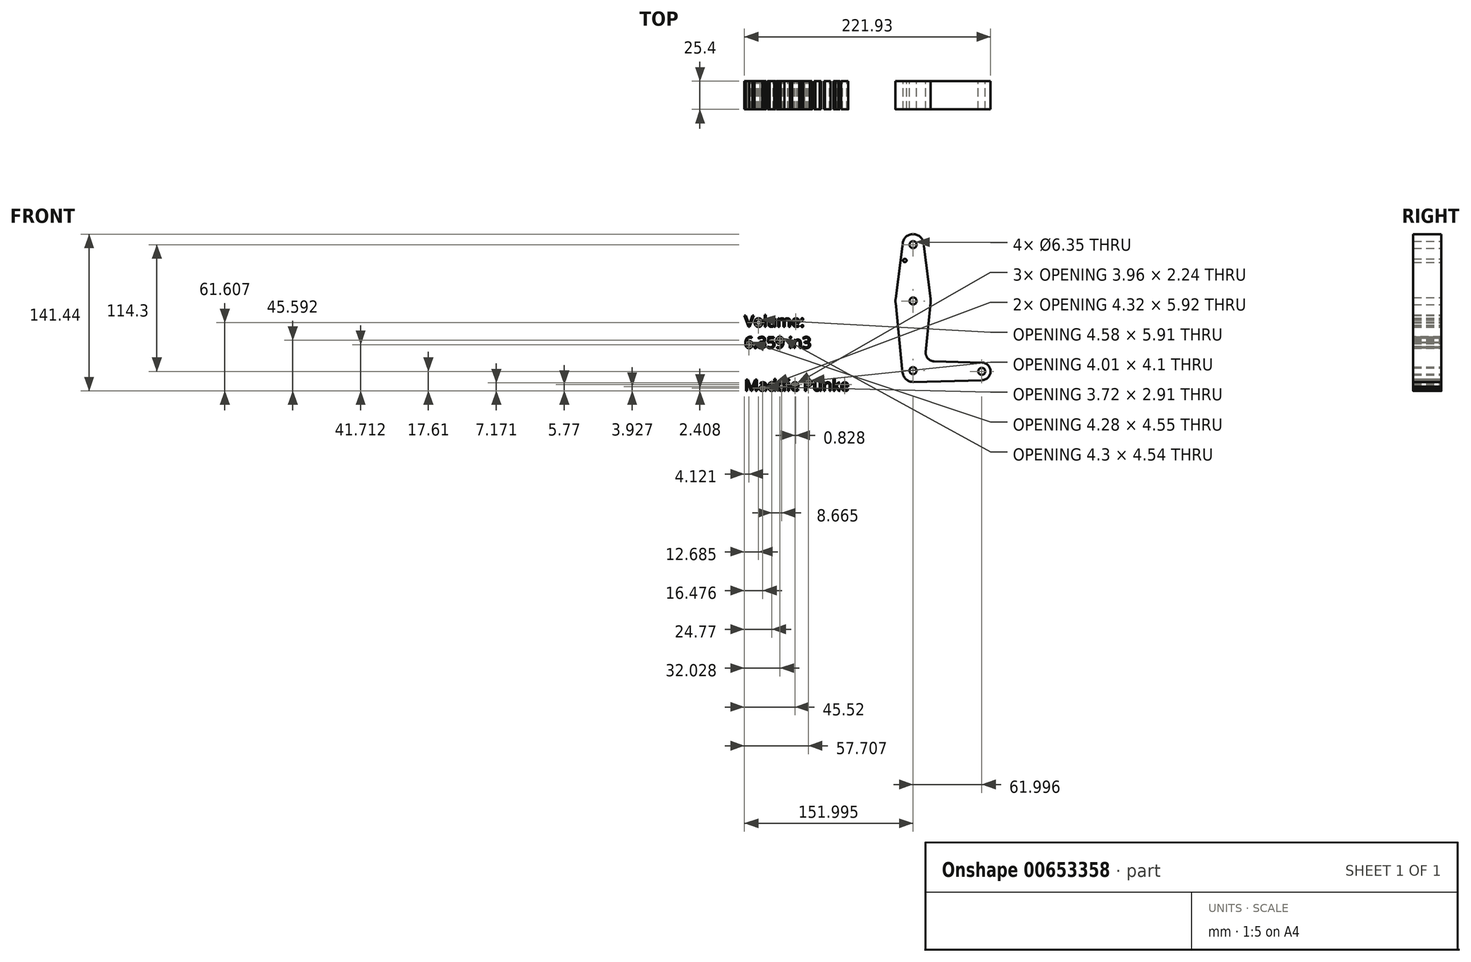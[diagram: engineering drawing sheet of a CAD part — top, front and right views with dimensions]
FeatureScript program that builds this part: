
annotation { "Feature Type Name" : "Feature", "Feature Type Description" : "" }
export const myFeature = defineFeature(function(context is Context, id is Id, definition is map)
    precondition{}
    {
        {
            var Q0;
            Q0=qCreatedBy(makeId("Front.planeOp"),FACE);
            var sketch = newSketch(context, id + "F0", { "sketchPlane" : qUnion([Q0])});
            skLineSegment(sketch, "E0", {"start": v(-2.44, 74.08) * mm, "end": v(-2.44, -40.22) * mm});
            skLineSegment(sketch, "E1", {"start": v(-2.44, -40.22) * mm, "end": v(59.47, -40.22) * mm});
            skCircle(sketch, "E2", {"center": v(-2.44, 74.08) * mm, "radius": 9.53 * mm});
            skCircle(sketch, "E3", {"center": v(-2.44, 23.28) * mm, "radius": 15.88 * mm});
            skCircle(sketch, "E4", {"center": v(-2.44, -40.22) * mm, "radius": 9.53 * mm});
            skCircle(sketch, "E5", {"center": v(59.47, -40.22) * mm, "radius": 7.94 * mm});
            skLineSegment(sketch, "E6", {"start": v(-11.9, 75.27) * mm, "end": v(-18.2, 25.26) * mm});
            skLineSegment(sketch, "E7", {"start": v(-18.24, 21.7) * mm, "end": v(-11.92, -41.17) * mm});
            skLineSegment(sketch, "E8", {"start": v(-2.2, -49.74) * mm, "end": v(59.67, -48.15) * mm});
            skCircle(sketch, "E9", {"center": v(-2.44, 74.08) * mm, "radius": 3.18 * mm});
            skCircle(sketch, "E10", {"center": v(-2.44, 23.28) * mm, "radius": 3.18 * mm});
            skCircle(sketch, "E11", {"center": v(-2.53, -39.56) * mm, "radius": 3.18 * mm});
            skCircle(sketch, "E12", {"center": v(59.47, -40.22) * mm, "radius": 3.18 * mm});
            skCircle(sketch, "E13", {"center": v(-9.93, 59.8) * mm, "radius": 1.59 * mm});
            skLineSegment(sketch, "E14", {"start": v(7, 75.27) * mm, "end": v(13.3, 25.26) * mm});
            skPoint(sketch, "E15.end.orphan", {"position": v(13.3, 25.26) * mm});
            skLineSegment(sketch, "E16", {"start": v(13.35, 21.7) * mm, "end": v(8.92, -22.44) * mm});
            skPoint(sketch, "E17.start.orphan", {"position": v(13.3, 21.25) * mm});
            skLineSegment(sketch, "E18", {"start": v(16.62, -31.18) * mm, "end": v(59.67, -32.28) * mm});
            skArc(sketch, "E19.filletArc", {"start": v(8.92, -22.44) * mm, "mid": v(10.86, -28.5) * mm, "end": v(16.62, -31.18) * mm});
            skText(sketch, "E20", { "text": "Volume:\n6.359 in3\n\nMaddie Punke ", "fontName": "OpenSans-Regular.ttf"});
            const initialGuessF0  = {"E20": [-0.15452, 0, 1, 0, 0.01018]};
            skSetInitialGuess(sketch, initialGuessF0);
            skSolve(sketch);
        }
        {
            var Q0;
            Q0 = qSketchRegion(id + "F0", true);
            var Q1;
            {var subQ0=sQuery(id+"F0.wireOp",EDGE,"E4");var subQ1=sQuery(id+"F0.wireOp",EDGE,"E0");var subQ2=makeQuery(id+"F0.imprint","INTERSECT",VERTEX,{"derivedFrom":[subQ1,subQ0]});Q1=makeQuery(id+"F0.imprint","IMPRINT",FACE,{"disambiguationData":[TD([[makeQuery(id+"F0.imprint","IMPRINT",EDGE,{"disambiguationData":[TD([[subQ2,-1.0]])],"derivedFrom":subQ1}),1.0]])]});}
            extrude(context, id + "F1", {"entities" : qUnion([Q0, Q1]), "depth" : 25.4 * mm, "offsetDistance" : 25.4 * mm});
        }
    });
